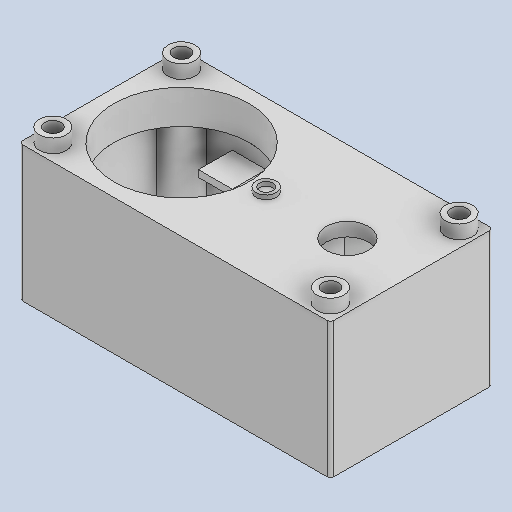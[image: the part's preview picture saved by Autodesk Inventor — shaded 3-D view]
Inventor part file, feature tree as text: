
AUTODESK INVENTOR PART (.ipt)
format: ipt  version: 2025.2 (Build 292293000, 293)  size: 167,424 bytes
history: native  units: mm
features: other x1, fillet x1
ambient origin geometry x8: Origin, YZ Plane, XZ Plane, XY Plane, X Axis, Y Axis, Z Axis, Center Point
bodies: Body1 (feature_tree)
feature tree (2):
  other  "Bryła1"
  fillet  "Fillet1"  [1 undecoded]
note: 1 required parameter value undecoded (feature->parameter linkage not recoverable at this tier; creation-order binding heuristic only, values carry confidence <= 0.55)
